# Revit family: SH-2003-14C,S
name_source: partatom
category: Lighting Fixtures
revit_build: Autodesk Revit 2017 (Build: 20160225_1515(x64)
units: mm (PartAtom-declared; Revit-internal decimal feet)

## family parameters
Always vertical = Yes
Cut with Voids When Loaded = No
Light Source = No
OmniClass Number = 23.80.70.00
OmniClass Title = Lighting
Part Type = Normal
Room Calculation Point = No
Round Connector Dimension = Use Diameter
Shared = No
Work Plane-Based = No

## types (2) — shared parameters
Body Material = Aluminium
Body color = Black
Cutting Diameter = 8 cm
Diameter = 11 cm
Flicker = FREE Flicker
Height = 12 cm
IP = IP65
Lamp = LED
Manufacturer = SHOA
Model = SH-2003-14c
Protection Class = Class I
Type medule = smd
URL = https://www.shoaco.com
Voltage/Frequency = 230V-50HZ
color rendering index(CRI) = 80
consumption current = 0 A
instalation = inground
website = www.shoaco.com

## per-type parameters (varying)
| type | color temperature | wattage. |
| SH-2003-14s(Aluminium body-3000K-GU10) | 3000K | 0 W |
| SH-2003-14s(Aluminium body-6500K-GU10) | 6500K | 7 W |

## geometry (parser evidence)
native form markers: Sweep x3
no freeform markers — native parametric forms only
